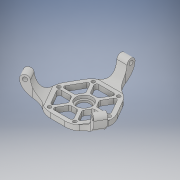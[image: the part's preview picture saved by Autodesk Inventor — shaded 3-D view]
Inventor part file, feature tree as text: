
AUTODESK INVENTOR PART (.ipt)
format: ipt  version: 2019.4 (Build 234330000, 330)  size: 381,952 bytes
history: native  units: mm
features: extrude x6, sketch x6, fillet x4, pattern_circular x3, plane x2
ambient origin geometry x8: Origin, YZ Plane, XZ Plane, XY Plane, X Axis, Y Axis, Z Axis, Center Point
bodies: Solid1 (feature_tree)
feature tree (21):
  extrude  "Extrusion1"  Depth=25.980762mm
  plane  "Work Plane2"
  extrude  "Extrusion3"  Depth=5.0mm TaperAngle=30.0deg
  fillet  "Fillet1"  Radius=15.5mm
  extrude  "Extrusion4"  Depth=20.0mm
  pattern_circular  "Circular Pattern1"  [2 undecoded]
  fillet  "Fillet2"  Radius=10.0mm
  extrude  "Extrusion5"  Depth=3.0mm
  pattern_circular  "Circular Pattern2"  [2 undecoded]
  fillet  "Fillet3"  Radius=30.0mm
  pattern_circular  "Circular Pattern3"  [2 undecoded]
  fillet  "Fillet4"  Radius=4.0mm
  extrude  "Extrusion6"  TaperAngle=30.0deg  [1 undecoded]
  extrude  "Extrusion7"  Depth=3.0mm
  sketch  "Sketch1"  dims[d0=30.0mm d1=25.980762mm]
  plane  "Work Plane1"
  sketch  "Sketch4"  dims[d2=5.0mm d3=0.0mm d7=30.0deg d14=15.0mm d15=15.5mm]
  sketch  "Sketch5"  dims[d16=90.0deg d17=20.0mm]
  sketch  "Sketch6"  dims[d18=90.0deg]
  sketch  "Sketch7"  dims[d19=4.0mm]
  sketch  "Sketch10"  dims[d20=8.0mm d21=10.0mm d22=0.0mm d23=10.0mm d24=12.0mm d25=10.0mm d26=0.0mm d27=30.0mm d28=360.0deg d30=10.0mm d31=4.0mm d32=30.0deg d33=11.0mm d34=60.0deg d35=11.0mm d36=120.0deg d37=12.0mm d38=30.0deg d39=4.0mm d40=4.0mm d41=10.0mm d42=0.0mm d43=60.0mm d44=360.0deg d46=2.0mm d47=60.0mm d48=360.0deg d50=20.0mm d51=25.0mm d52=3.5mm d53=60.0mm d55=360.0deg d57=10.0mm d58=0.0mm d59=16.0mm d60=3.0mm d61=0.0mm]
note: 7 required parameter values undecoded (feature->parameter linkage not recoverable at this tier; creation-order binding heuristic only, values carry confidence <= 0.55)
